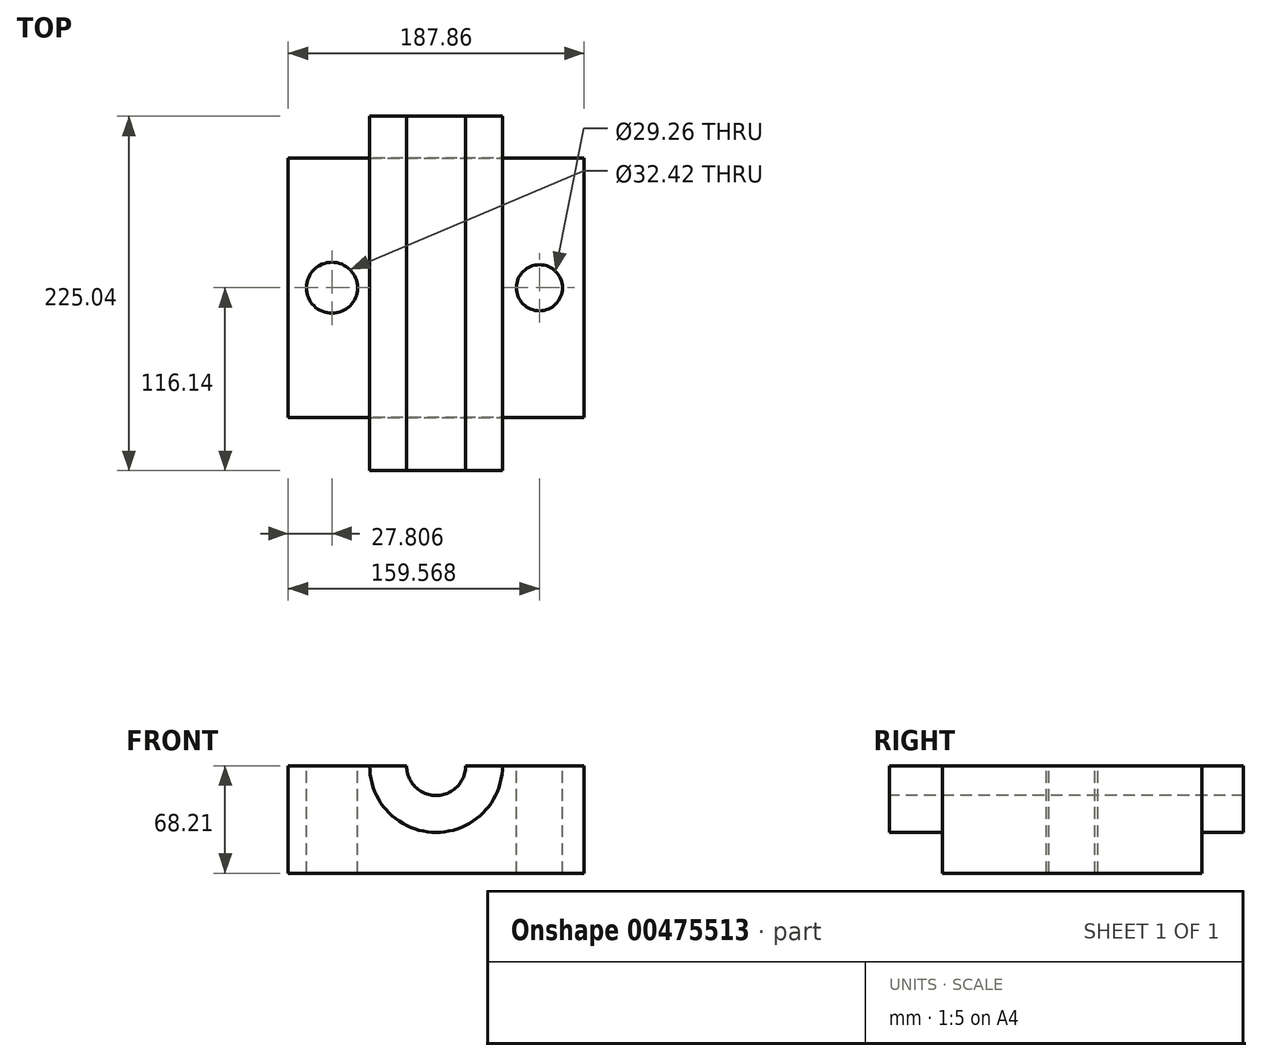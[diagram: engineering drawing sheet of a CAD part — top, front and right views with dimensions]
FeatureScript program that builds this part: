
annotation { "Feature Type Name" : "Feature", "Feature Type Description" : "" }
export const myFeature = defineFeature(function(context is Context, id is Id, definition is map)
    precondition{}
    {
        {
            var Q0;
            Q0=qCreatedBy(makeId("Top.planeOp"),FACE);
            var sketch = newSketch(context, id + "F0", { "sketchPlane" : qUnion([Q0])});
            skLineSegment(sketch, "E0.bottom", {"start": v(93.93, 82.36) * mm, "end": v(-93.93, 82.36) * mm});
            skLineSegment(sketch, "E0.top", {"start": v(93.93, -82.36) * mm, "end": v(-93.93, -82.36) * mm});
            skLineSegment(sketch, "E0.left", {"start": v(93.93, 82.36) * mm, "end": v(93.93, -82.36) * mm});
            skLineSegment(sketch, "E0.right", {"start": v(-93.93, 82.36) * mm, "end": v(-93.93, -82.36) * mm});
            skPoint(sketch, "E0.middle", {"position": v(0, 0) * mm});
            skSolve(sketch);
        }
        {
            var Q0;
            Q0 = qSketchRegion(id + "F0", true);
            extrude(context, id + "F1", {"entities" : qUnion([Q0]), "depth" : 50.8 * mm, "symmetric" : true});
        }
        {
            var Q0;
            Q0=makeQuery(id+"F1.opExtrude","CAP_FACE",FACE,{"disambiguationData":[OSD([sQuery(id+"F0.wireOp",EDGE,"E0.bottom"),sQuery(id+"F0.wireOp",EDGE,"E0.top"),sQuery(id+"F0.wireOp",EDGE,"E0.left"),sQuery(id+"F0.wireOp",EDGE,"E0.right")])],"isStart":false});
            extrude(context, id + "F2", {"entities" : qUnion([Q0]), "operationType" : NewBodyOperationType.ADD, "depth" : 34.54 * mm, "symmetric" : true});
        }
        {
            var Q0;
            {var subQ0=sQuery(id+"F0.wireOp",EDGE,"E0.top");Q0=makeQuery(id+"F2.boolean.opBoolean","MERGE",FACE,{"derivedFrom":[makeQuery(id+"F1.opExtrude","SWEPT_FACE",FACE,{"disambiguationData":[OSD([subQ0])]}),makeQuery(id+"F2.opExtrude","SWEPT_FACE",FACE,{"disambiguationData":[OSD([subQ0])]})]});}
            var sketch = newSketch(context, id + "F3", { "sketchPlane" : qUnion([Q0])});
            skCircle(sketch, "E1", {"center": v(0, 42.67) * mm, "radius": 42.16 * mm});
            skCircle(sketch, "E2", {"center": v(0, 42.67) * mm, "radius": 18.72 * mm});
            skSolve(sketch);
        }
        {
            var Q0;
            Q0 = qSketchRegion(id + "F3", true);
            var Q1;
            {var subQ0=sQuery(id+"F0.wireOp",EDGE,"E0.bottom");Q1=makeQuery(id+"F2.boolean.opBoolean","MERGE",FACE,{"derivedFrom":[makeQuery(id+"F1.opExtrude","SWEPT_FACE",FACE,{"disambiguationData":[OSD([subQ0])]}),makeQuery(id+"F2.opExtrude","SWEPT_FACE",FACE,{"disambiguationData":[OSD([subQ0])]})]});}
            extrude(context, id + "F4", {"entities" : qUnion([Q0]), "operationType" : NewBodyOperationType.ADD, "oppositeDirection" : true, "endBoundEntityFace" : qUnion([Q1]), "depth" : 191.26 * mm, "hasSecondDirection" : true, "secondDirectionOppositeDirection" : false, "secondDirectionDepth" : 33.78 * mm});
        }
        {
            var Q0;
            {var subQ0=sQuery(id+"F3.wireOp",EDGE,"E2");var subQ1=makeQuery(id+"F2.opExtrude","CAP_EDGE",EDGE,{"disambiguationData":[OSD([sQuery(id+"F0.wireOp",EDGE,"E0.top")])],"isStart":false});var subQ2=makeQuery(id+"F3.imprint","INTERSECT",VERTEX,{"disambiguationData":[OD(0.0)],"derivedFrom":[subQ1,subQ0]});Q0=makeQuery(id+"F3.imprint","IMPRINT",FACE,{"disambiguationData":[TD([[makeQuery(id+"F3.imprint","IMPRINT",EDGE,{"disambiguationData":[TD([[subQ2,1.0]])],"derivedFrom":subQ0}),1.0]])]});}
            extrude(context, id + "F5", {"entities" : qUnion([Q0]), "operationType" : NewBodyOperationType.REMOVE, "endBound" : BoundingType.THROUGH_ALL, "oppositeDirection" : true, "depth" : 25.4 * mm});
        }
        {
            var Q0;
            {var subQ0=sQuery(id+"F3.wireOp",EDGE,"E1");var subQ1=makeQuery(id+"F2.opExtrude","CAP_EDGE",EDGE,{"disambiguationData":[OSD([sQuery(id+"F0.wireOp",EDGE,"E0.top")])],"isStart":false});var subQ2=makeQuery(id+"F3.imprint","INTERSECT",VERTEX,{"disambiguationData":[OD(0.0)],"derivedFrom":[subQ1,subQ0]});Q0=makeQuery(id+"F3.imprint","IMPRINT",FACE,{"disambiguationData":[TD([[makeQuery(id+"F3.imprint","IMPRINT",EDGE,{"disambiguationData":[TD([[subQ2,-1.0]])],"derivedFrom":subQ0}),1.0]])]});}
            var sketch = newSketch(context, id + "F6", { "sketchPlane" : qUnion([Q0])});
            skLineSegment(sketch, "E3", {"start": v(0, 42.81) * mm, "end": v(-50.25, 42.81) * mm});
            skLineSegment(sketch, "E4", {"start": v(-50.25, 42.81) * mm, "end": v(-50.25, 85.44) * mm});
            skLineSegment(sketch, "E5", {"start": v(-50.25, 85.44) * mm, "end": v(50.01, 85.44) * mm});
            skLineSegment(sketch, "E6", {"start": v(50.01, 85.44) * mm, "end": v(50.01, 42.81) * mm});
            skLineSegment(sketch, "E7", {"start": v(50.01, 42.81) * mm, "end": v(0, 42.81) * mm});
            skSolve(sketch);
        }
        {
            var Q0;
            Q0 = qSketchRegion(id + "F6", true);
            extrude(context, id + "F7", {"entities" : qUnion([Q0]), "operationType" : NewBodyOperationType.REMOVE, "endBound" : BoundingType.THROUGH_ALL, "oppositeDirection" : true, "depth" : 25.4 * mm, "hasSecondDirection" : true, "secondDirectionOppositeDirection" : false, "secondDirectionDepth" : 101.6 * mm});
        }
        {
            var Q0;
            {var subQ0=sQuery(id+"F0.wireOp",EDGE,"E0.bottom");var subQ1=sQuery(id+"F0.wireOp",EDGE,"E0.top");var subQ2=sQuery(id+"F0.wireOp",EDGE,"E0.right");Q0=makeQuery(id+"F4.boolean.opBoolean","SPLIT",FACE,{"disambiguationData":[TD([makeQuery(id+"F1.opExtrude","SWEPT_FACE",FACE,{"disambiguationData":[OSD([subQ2])]})])],"derivedFrom":makeQuery(id+"F2.opExtrude","CAP_FACE",FACE,{"disambiguationData":[OSD([subQ0,subQ1,sQuery(id+"F0.wireOp",EDGE,"E0.left"),subQ2])],"isStart":false})});}
            var sketch = newSketch(context, id + "F8", { "sketchPlane" : qUnion([Q0])});
            skCircle(sketch, "E8", {"center": v(-66.12, 0) * mm, "radius": 16.2 * mm});
            skCircle(sketch, "E9", {"center": v(65.64, 0) * mm, "radius": 14.63 * mm});
            skSolve(sketch);
        }
        {
            var Q0;
            Q0 = qSketchRegion(id + "F8", true);
            extrude(context, id + "F9", {"entities" : qUnion([Q0]), "operationType" : NewBodyOperationType.REMOVE, "endBound" : BoundingType.THROUGH_ALL, "oppositeDirection" : true, "depth" : 25.4 * mm});
        }
    });
